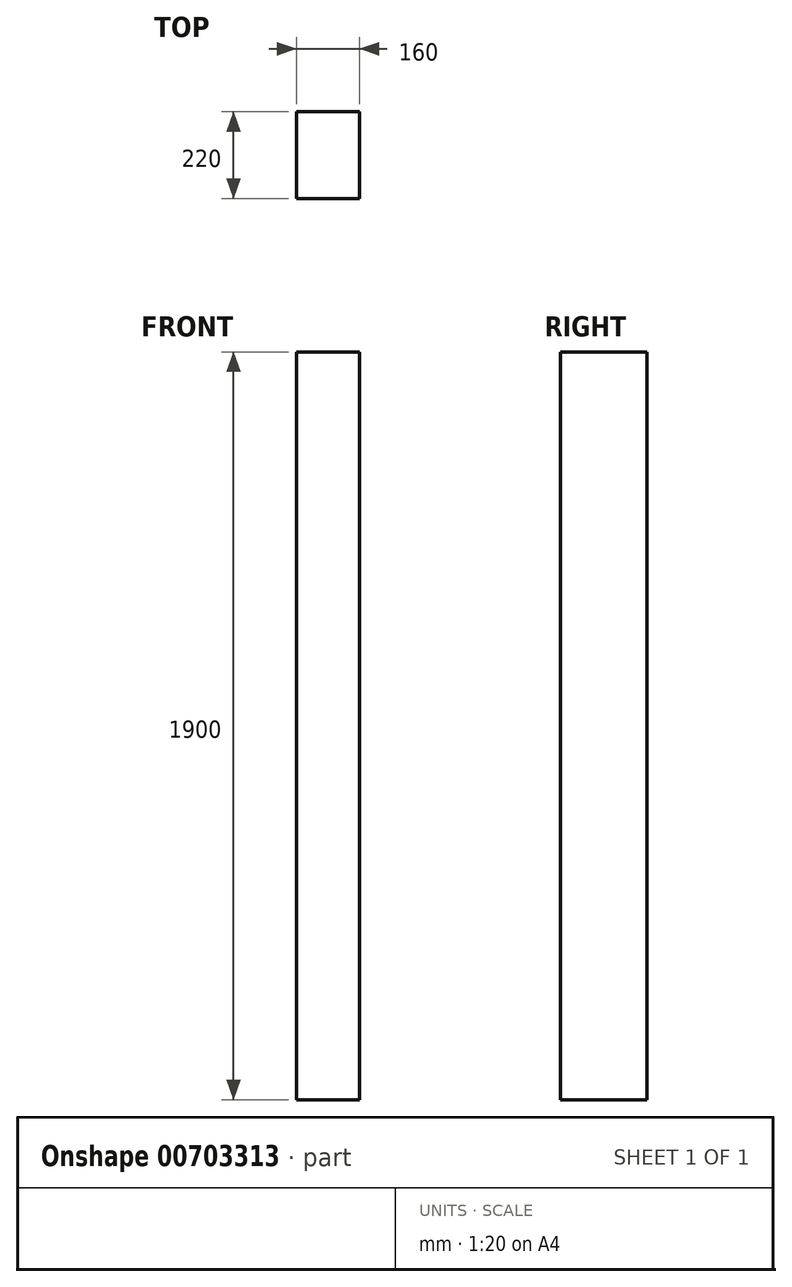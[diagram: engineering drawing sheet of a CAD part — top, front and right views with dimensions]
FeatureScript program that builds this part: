
annotation { "Feature Type Name" : "Feature", "Feature Type Description" : "" }
export const myFeature = defineFeature(function(context is Context, id is Id, definition is map)
    precondition{}
    {
        {
            var Q0;
            Q0=qCreatedBy(makeId("Top.planeOp"),FACE);
            var sketch = newSketch(context, id + "F0", { "sketchPlane" : qUnion([Q0])});
            skLineSegment(sketch, "E0.bottom", {"start": v(-81.88, 184.8) * mm, "end": v(78.12, 184.8) * mm});
            skLineSegment(sketch, "E0.top", {"start": v(-81.88, -35.2) * mm, "end": v(78.12, -35.2) * mm});
            skLineSegment(sketch, "E0.left", {"start": v(-81.88, 184.8) * mm, "end": v(-81.88, -35.2) * mm});
            skLineSegment(sketch, "E0.right", {"start": v(78.12, 184.8) * mm, "end": v(78.12, -35.2) * mm});
            skSolve(sketch);
        }
        {
            var Q0;
            Q0=makeQuery(id+"F0.imprint","IMPRINT",FACE,{"disambiguationData":[TD([[makeQuery(id+"F0.imprint","IMPRINT",EDGE,{"derivedFrom":sQuery(id+"F0.wireOp",EDGE,"E0.bottom")}),-1.0]])]});
            extrude(context, id + "F1", {"entities" : qUnion([Q0]), "depth" : 1900 * mm, "offsetDistance" : 25 * mm});
        }
    });
